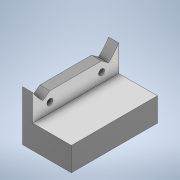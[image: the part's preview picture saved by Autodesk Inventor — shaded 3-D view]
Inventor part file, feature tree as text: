
AUTODESK INVENTOR PART (.ipt)
format: ipt  version: 2022 (Build 260153000, 153)  size: 1,087,488 bytes
history: mixed  units: mm
features: sketch x6, extrude x5, other x3, imported_body x1
ambient origin geometry x8: Origin, YZ Plane, XZ Plane, XY Plane, X Axis, Y Axis, Z Axis, Center Point
bodies: Solid1 (imported_parasolid)
feature tree (15):
  other  "Assembly2.iam"
  other  "96Gears_Stage_1_modified.ipt:1"
  other  "96Gears_Stage_2_modified.ipt:1"
  extrude  "Extrusion3"  Depth=10.0mm
  extrude  "Extrusion5"  Depth=18.0mm TaperAngle=0.0deg
  extrude  "Extrusion6"  Depth=6.0mm TaperAngle=0.0deg
  extrude  "Extrusion7"  Depth=10.0mm TaperAngle=0.0deg
  extrude  "Extrusion8"  Depth=4.1mm
  sketch  "Sketch5"  dims[d7=6.0mm d8=18.0mm d9=0.0mm]
  sketch  "Sketch4"  dims[d0=10.0mm d6=3.0mm]
  sketch  "Sketch7"  dims[d17=32.25mm d18=6.0mm d19=0.0mm]
  sketch  "Sketch8"  dims[d20=10.0mm d21=10.0mm d22=0.0mm]
  sketch  "Sketch9"  dims[d24=4.1mm d25=4.1mm]
  sketch  "Sketch10"  dims[d26=10.0mm d27=0.0mm d28=7.0mm d29=0.0mm d30=0.0mm]
  imported_body  NMx_Import_Brep_tag  [imported B-rep: ~14 faces, bbox_mm=[34.0, 35.0, 60.0]]
